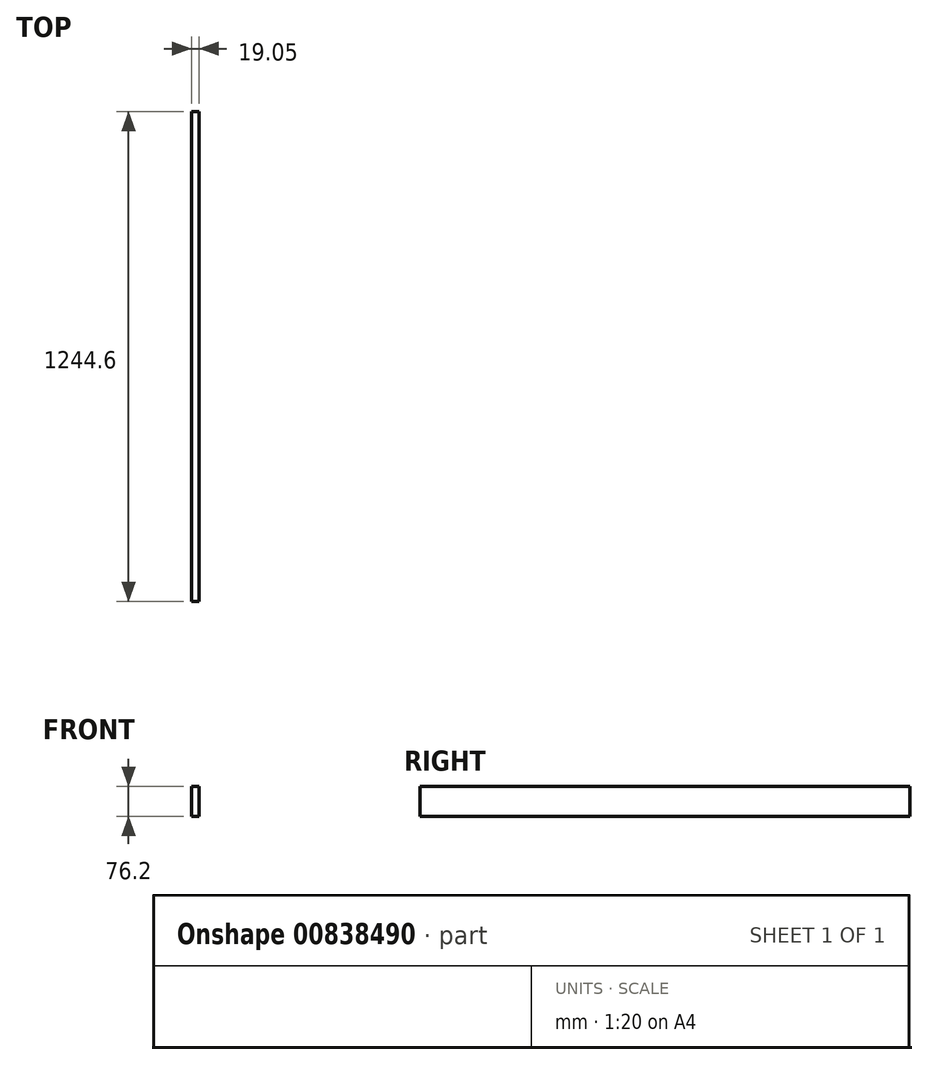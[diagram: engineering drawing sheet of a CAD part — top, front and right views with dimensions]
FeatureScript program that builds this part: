
annotation { "Feature Type Name" : "Feature", "Feature Type Description" : "" }
export const myFeature = defineFeature(function(context is Context, id is Id, definition is map)
    precondition{}
    {
        {
            var Q0;
            Q0=qCreatedBy(makeId("Right.planeOp"),FACE);
            var sketch = newSketch(context, id + "F0", { "sketchPlane" : qUnion([Q0])});
            skLineSegment(sketch, "E0.bottom", {"start": v(-622.3, -38.1) * mm, "end": v(622.3, -38.1) * mm});
            skLineSegment(sketch, "E0.top", {"start": v(-622.3, 38.1) * mm, "end": v(622.3, 38.1) * mm});
            skLineSegment(sketch, "E0.left", {"start": v(-622.3, -38.1) * mm, "end": v(-622.3, 38.1) * mm});
            skLineSegment(sketch, "E0.right", {"start": v(622.3, -38.1) * mm, "end": v(622.3, 38.1) * mm});
            skPoint(sketch, "E0.middle", {"position": v(0, 0) * mm});
            skSolve(sketch);
        }
        {
            var Q0;
            Q0 = qSketchRegion(id + "F0", true);
            extrude(context, id + "F1", {"entities" : qUnion([Q0]), "depth" : 19.05 * mm, "offsetDistance" : 25.4 * mm});
        }
    });
